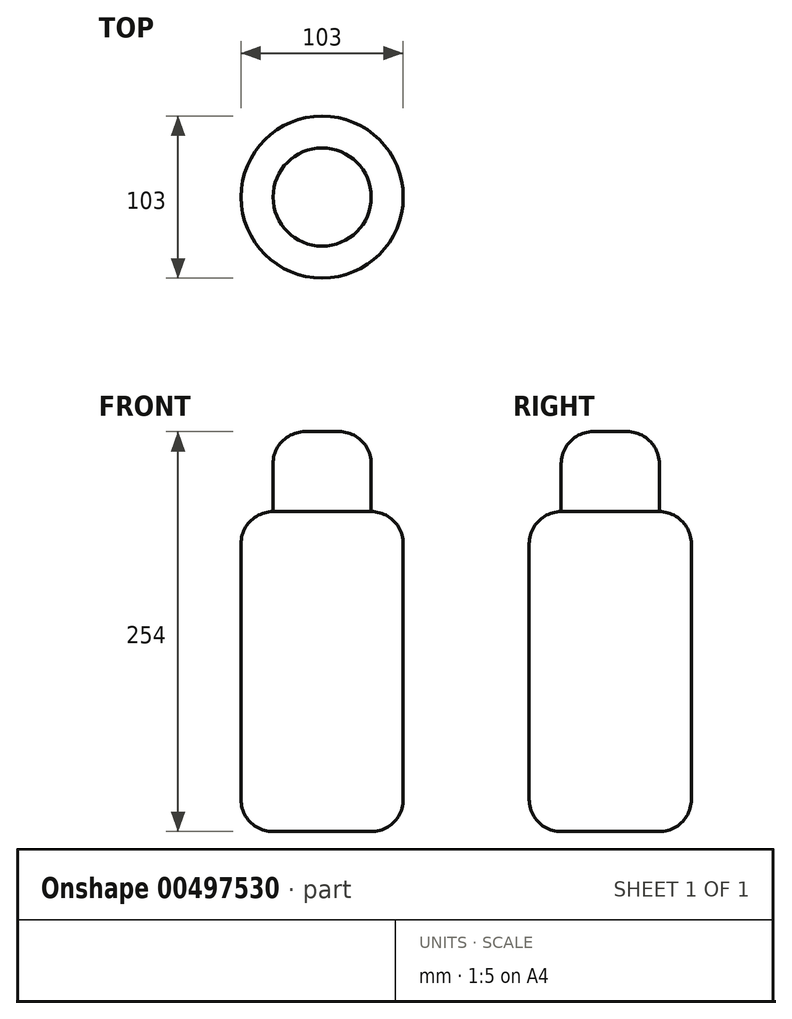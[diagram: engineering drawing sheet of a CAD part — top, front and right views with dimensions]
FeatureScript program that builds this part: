
annotation { "Feature Type Name" : "Feature", "Feature Type Description" : "" }
export const myFeature = defineFeature(function(context is Context, id is Id, definition is map)
    precondition{}
    {
        {
            var Q0;
            Q0=qCreatedBy(makeId("Top.planeOp"),FACE);
            var sketch = newSketch(context, id + "F0", { "sketchPlane" : qUnion([Q0])});
            skCircle(sketch, "E0", {"center": v(0, 0) * mm, "radius": 51.5 * mm});
            skSolve(sketch);
        }
        {
            var Q0;
            Q0=makeQuery(id+"F0.imprint","IMPRINT",FACE,{"disambiguationData":[TD([[makeQuery(id+"F0.imprint","IMPRINT",EDGE,{"derivedFrom":sQuery(id+"F0.wireOp",EDGE,"E0")}),1.0]])]});
            extrude(context, id + "F1", {"entities" : qUnion([Q0]), "depth" : 203.2 * mm});
        }
        {
            var Q0;
            Q0=makeQuery(id+"F1.opExtrude","CAP_FACE",FACE,{"disambiguationData":[OSD([sQuery(id+"F0.wireOp",EDGE,"E0")])],"isStart":true});
            var Q1;
            Q1=makeQuery(id+"F1.opExtrude","CAP_FACE",FACE,{"disambiguationData":[OSD([sQuery(id+"F0.wireOp",EDGE,"E0")])],"isStart":false});
            fillet(context, id + "F2", {"entities" : qUnion([Q0, Q1]), "radius" : 20.32 * mm, "tangentPropagation" : true, "allowEdgeOverflow" : false});
        }
        {
            var Q0;
            Q0=makeQuery(id+"F1.opExtrude","CAP_FACE",FACE,{"disambiguationData":[OSD([sQuery(id+"F0.wireOp",EDGE,"E0")])],"isStart":false});
            extrude(context, id + "F3", {"entities" : qUnion([Q0]), "operationType" : NewBodyOperationType.ADD, "depth" : 50.8 * mm});
        }
        {
            var Q0;
            Q0=makeQuery(id+"F3.opExtrude","CAP_FACE",FACE,{"disambiguationData":[OSD([sQuery(id+"F0.wireOp",EDGE,"E0")])],"isStart":false});
            fillet(context, id + "F4", {"entities" : qUnion([Q0]), "radius" : 20.32 * mm, "tangentPropagation" : true, "allowEdgeOverflow" : false});
        }
    });
